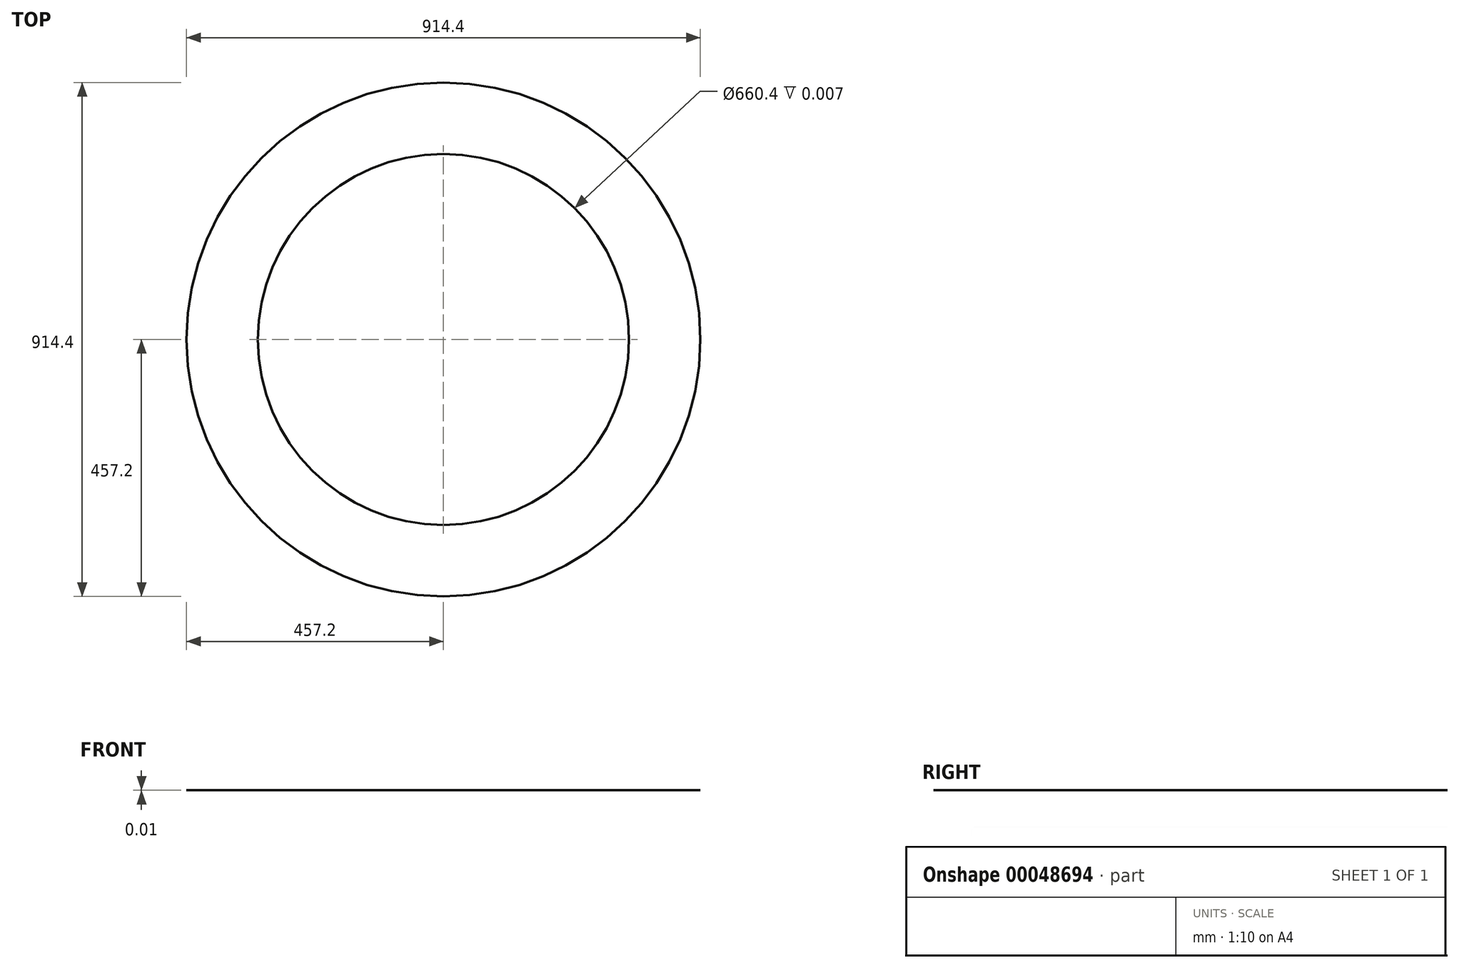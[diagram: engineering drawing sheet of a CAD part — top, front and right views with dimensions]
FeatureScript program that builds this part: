
annotation { "Feature Type Name" : "Feature", "Feature Type Description" : "" }
export const myFeature = defineFeature(function(context is Context, id is Id, definition is map)
    precondition{}
    {
        {
            var Q0;
            Q0=qCreatedBy(makeId("Top.planeOp"),FACE);
            var sketch = newSketch(context, id + "F0", { "sketchPlane" : qUnion([Q0])});
            skCircle(sketch, "E0", {"center": v(0, 0) * mm, "radius": 457.2 * mm});
            skCircle(sketch, "E1", {"center": v(0, 0) * mm, "radius": 330.2 * mm});
            skSolve(sketch);
        }
        {
            var Q0;
            Q0 = qSketchRegion(id + "F0", true);
            extrude(context, id + "F1", {"entities" : qUnion([Q0]), "depth" : 3 / 457.2 * mm});
        }
    });
